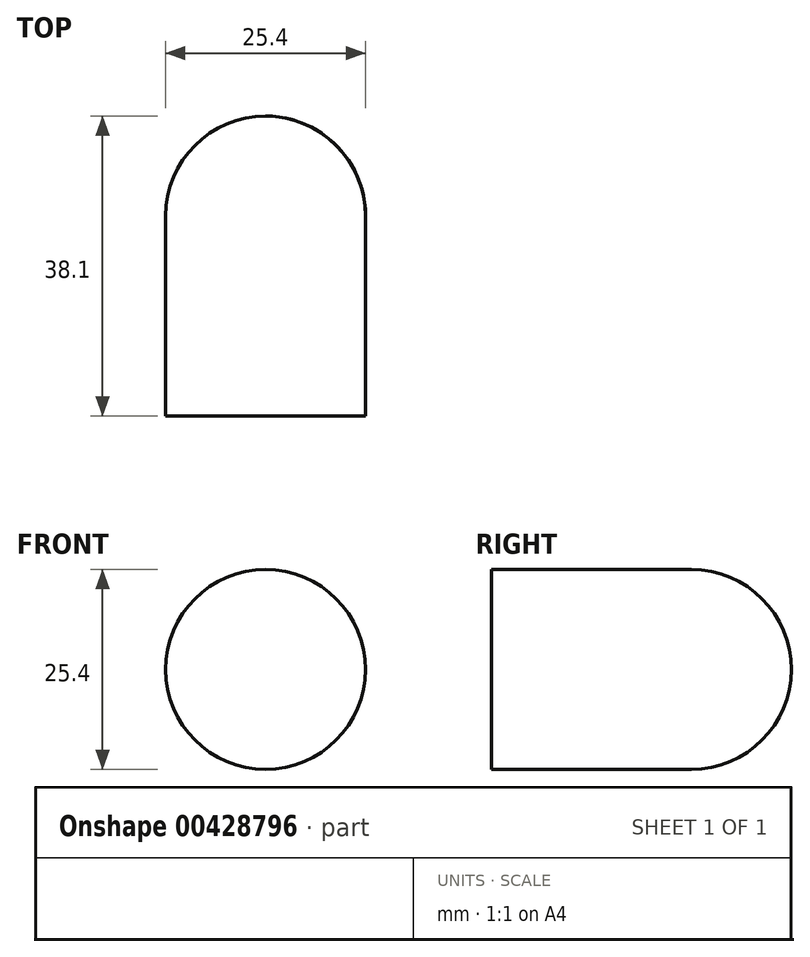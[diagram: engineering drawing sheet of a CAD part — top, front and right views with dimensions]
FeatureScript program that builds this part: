
annotation { "Feature Type Name" : "Feature", "Feature Type Description" : "" }
export const myFeature = defineFeature(function(context is Context, id is Id, definition is map)
    precondition{}
    {
        {
            var Q0;
            Q0=qCreatedBy(makeId("Top.planeOp"),FACE);
            var sketch = newSketch(context, id + "F0", { "sketchPlane" : qUnion([Q0])});
            skLineSegment(sketch, "E0", {"start": v(0, 0) * mm, "end": v(0, 159.77) * mm, "construction": true});
            skLineSegment(sketch, "E1", {"start": v(0, 0) * mm, "end": v(0, 38.1) * mm});
            skArc(sketch, "E2", {"start": v(12.7, 25.4) * mm, "mid": v(8.98, 34.38) * mm, "end": v(0, 38.1) * mm});
            skLineSegment(sketch, "E3", {"start": v(12.7, 25.4) * mm, "end": v(12.7, 0) * mm});
            skLineSegment(sketch, "E4", {"start": v(12.7, 0) * mm, "end": v(0, 0) * mm});
            skSolve(sketch);
        }
        {
            var Q0;
            Q0=makeQuery(id+"F0.imprint","IMPRINT",FACE,{"disambiguationData":[TD([[makeQuery(id+"F0.imprint","IMPRINT",EDGE,{"derivedFrom":sQuery(id+"F0.wireOp",EDGE,"E1")}),-1.0]])]});
            var Q1;
            Q1=sQuery(id+"F0.wireOp",EDGE,"E0");
            revolve(context, id + "F1", {"entities" : qUnion([Q0]), "axis" : qUnion([Q1]), "revolveType" : RevolveType.FULL});
        }
    });
